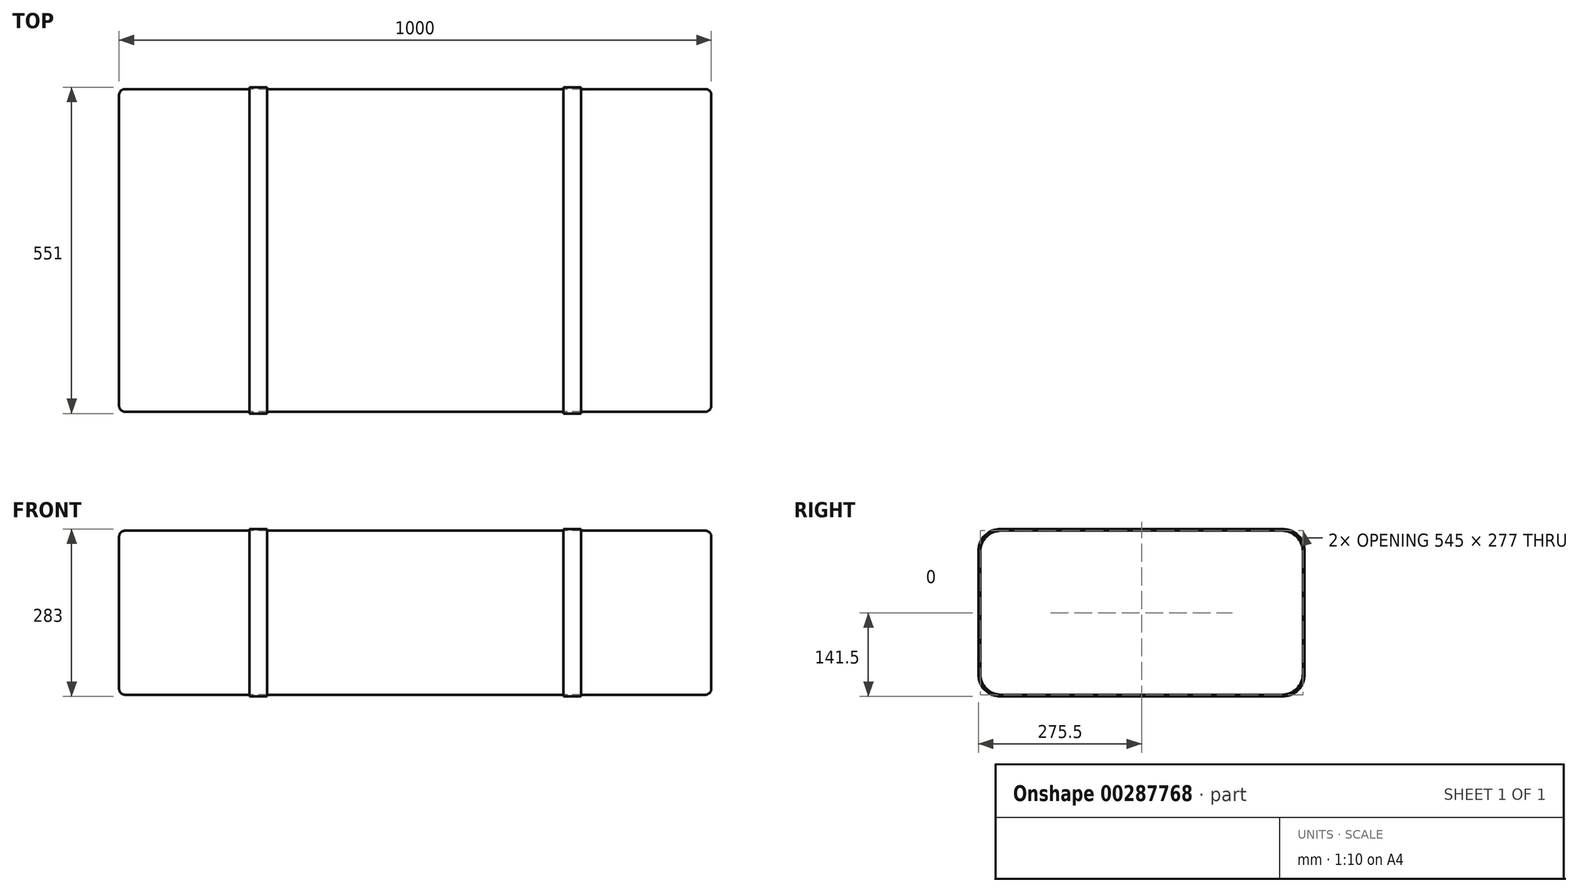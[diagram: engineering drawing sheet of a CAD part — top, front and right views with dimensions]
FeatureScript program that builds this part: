
annotation { "Feature Type Name" : "Feature", "Feature Type Description" : "" }
export const myFeature = defineFeature(function(context is Context, id is Id, definition is map)
    precondition{}
    {
        {
            var Q0;
            Q0=qCreatedBy(makeId("Top.planeOp"),FACE);
            cPlane(context, id + "F0", {"entities" : qUnion([Q0]), "cplaneType" : CPlaneType.OFFSET, "offset" : 250 * mm, "width" : 150 * mm, "height" : 150 * mm});
        }
        {
            var Q0;
            Q0=qCreatedBy(id+"F0.planeOp",FACE);
            var sketch = newSketch(context, id + "F1", { "sketchPlane" : qUnion([Q0])});
            skLineSegment(sketch, "E0.bottom", {"start": v(500, 272.5) * mm, "end": v(-500, 272.5) * mm});
            skLineSegment(sketch, "E0.top", {"start": v(500, -272.5) * mm, "end": v(-500, -272.5) * mm});
            skLineSegment(sketch, "E0.left", {"start": v(500, 272.5) * mm, "end": v(500, -272.5) * mm});
            skLineSegment(sketch, "E0.right", {"start": v(-500, 272.5) * mm, "end": v(-500, -272.5) * mm});
            skPoint(sketch, "E0.middle", {"position": v(0, 0) * mm});
            skSolve(sketch);
        }
        {
            var Q0;
            Q0 = qSketchRegion(id + "F1", true);
            extrude(context, id + "F2", {"entities" : qUnion([Q0]), "depth" : 277 * mm});
        }
        {
            var Q0;
            Q0=makeQuery(id+"F2.opExtrude","CAP_EDGE",EDGE,{"disambiguationData":[OSD([sQuery(id+"F1.wireOp",EDGE,"E0.top")])],"isStart":false});
            var Q1;
            Q1=makeQuery(id+"F2.opExtrude","CAP_EDGE",EDGE,{"disambiguationData":[OSD([sQuery(id+"F1.wireOp",EDGE,"E0.top")])],"isStart":true});
            var Q2;
            Q2=makeQuery(id+"F2.opExtrude","CAP_EDGE",EDGE,{"disambiguationData":[OSD([sQuery(id+"F1.wireOp",EDGE,"E0.bottom")])],"isStart":false});
            var Q3;
            Q3=makeQuery(id+"F2.opExtrude","CAP_EDGE",EDGE,{"disambiguationData":[OSD([sQuery(id+"F1.wireOp",EDGE,"E0.bottom")])],"isStart":true});
            fillet(context, id + "F3", {"entities" : qUnion([Q0, Q1, Q2, Q3]), "radius" : 35 * mm, "tangentPropagation" : true, "allowEdgeOverflow" : false});
        }
        {
            var Q0;
            Q0=makeQuery(id+"F2.opExtrude","CAP_EDGE",EDGE,{"disambiguationData":[OSD([sQuery(id+"F1.wireOp",EDGE,"E0.right")])],"isStart":false});
            var Q1;
            Q1=makeQuery(id+"F2.opExtrude","CAP_EDGE",EDGE,{"disambiguationData":[OSD([sQuery(id+"F1.wireOp",EDGE,"E0.left")])],"isStart":false});
            fillet(context, id + "F4", {"entities" : qUnion([Q0, Q1]), "radius" : 10 * mm, "tangentPropagation" : true, "allowEdgeOverflow" : false});
        }
        {
            var Q0;
            Q0=qCreatedBy(makeId("Right.planeOp"),FACE);
            cPlane(context, id + "F5", {"entities" : qUnion([Q0]), "cplaneType" : CPlaneType.OFFSET, "offset" : 250 * mm, "width" : 150 * mm, "height" : 150 * mm});
        }
        {
            var Q0;
            Q0=qCreatedBy(id+"F5.planeOp",FACE);
            var sketch = newSketch(context, id + "F6", { "sketchPlane" : qUnion([Q0])});
            skArc(sketch, "E1.0", {"start": v(-275.5, 492) * mm, "mid": v(-264.37, 518.87) * mm, "end": v(-237.5, 530) * mm});
            skLineSegment(sketch, "E1.1", {"start": v(-275.5, 285) * mm, "end": v(-275.5, 492) * mm});
            skLineSegment(sketch, "E1.2", {"start": v(-237.5, 530) * mm, "end": v(237.5, 530) * mm});
            skArc(sketch, "E1.3", {"start": v(-237.5, 247) * mm, "mid": v(-264.37, 258.13) * mm, "end": v(-275.5, 285) * mm});
            skArc(sketch, "E1.4", {"start": v(237.5, 530) * mm, "mid": v(264.37, 518.87) * mm, "end": v(275.5, 492) * mm});
            skLineSegment(sketch, "E1.5", {"start": v(275.5, 492) * mm, "end": v(275.5, 285) * mm});
            skArc(sketch, "E1.6", {"start": v(275.5, 285) * mm, "mid": v(264.37, 258.13) * mm, "end": v(237.5, 247) * mm});
            skLineSegment(sketch, "E1.7", {"start": v(237.5, 247) * mm, "end": v(-237.5, 247) * mm});
            skArc(sketch, "E2.0", {"start": v(-272.5, 492) * mm, "mid": v(-262.25, 516.75) * mm, "end": v(-237.5, 527) * mm});
            skLineSegment(sketch, "E2.1", {"start": v(-272.5, 285) * mm, "end": v(-272.5, 492) * mm});
            skLineSegment(sketch, "E2.2", {"start": v(-237.5, 527) * mm, "end": v(237.5, 527) * mm});
            skArc(sketch, "E2.3", {"start": v(-237.5, 250) * mm, "mid": v(-262.25, 260.25) * mm, "end": v(-272.5, 285) * mm});
            skArc(sketch, "E2.4", {"start": v(237.5, 527) * mm, "mid": v(262.25, 516.75) * mm, "end": v(272.5, 492) * mm});
            skLineSegment(sketch, "E2.5", {"start": v(272.5, 492) * mm, "end": v(272.5, 285) * mm});
            skArc(sketch, "E2.6", {"start": v(272.5, 285) * mm, "mid": v(262.25, 260.25) * mm, "end": v(237.5, 250) * mm});
            skLineSegment(sketch, "E2.7", {"start": v(237.5, 250) * mm, "end": v(-237.5, 250) * mm});
            skSolve(sketch);
        }
        {
            var Q0;
            Q0 = qSketchRegion(id + "F6", true);
            extrude(context, id + "F7", {"entities" : qUnion([Q0]), "depth" : 30 * mm});
        }
        {
            var Q0;
            Q0=makeQuery(id+"F7.opExtrude","SWEPT_BODY",BODY,{"disambiguationData":[OSD([sQuery(id+"F6.wireOp",EDGE,"E1.0"),sQuery(id+"F6.wireOp",EDGE,"E1.1"),sQuery(id+"F6.wireOp",EDGE,"E1.2"),sQuery(id+"F6.wireOp",EDGE,"E1.3"),sQuery(id+"F6.wireOp",EDGE,"E1.4"),sQuery(id+"F6.wireOp",EDGE,"E1.5"),sQuery(id+"F6.wireOp",EDGE,"E1.6"),sQuery(id+"F6.wireOp",EDGE,"E1.7"),sQuery(id+"F6.wireOp",EDGE,"E2.0"),sQuery(id+"F6.wireOp",EDGE,"E2.1"),sQuery(id+"F6.wireOp",EDGE,"E2.2"),sQuery(id+"F6.wireOp",EDGE,"E2.3"),sQuery(id+"F6.wireOp",EDGE,"E2.4"),sQuery(id+"F6.wireOp",EDGE,"E2.5"),sQuery(id+"F6.wireOp",EDGE,"E2.6"),sQuery(id+"F6.wireOp",EDGE,"E2.7")])]});
            var Q1;
            Q1=qCreatedBy(makeId("Right.planeOp"),FACE);
            mirror(context, id + "F8", {"entities" : qUnion([Q0]), "mirrorPlane" : qUnion([Q1])});
        }
    });
